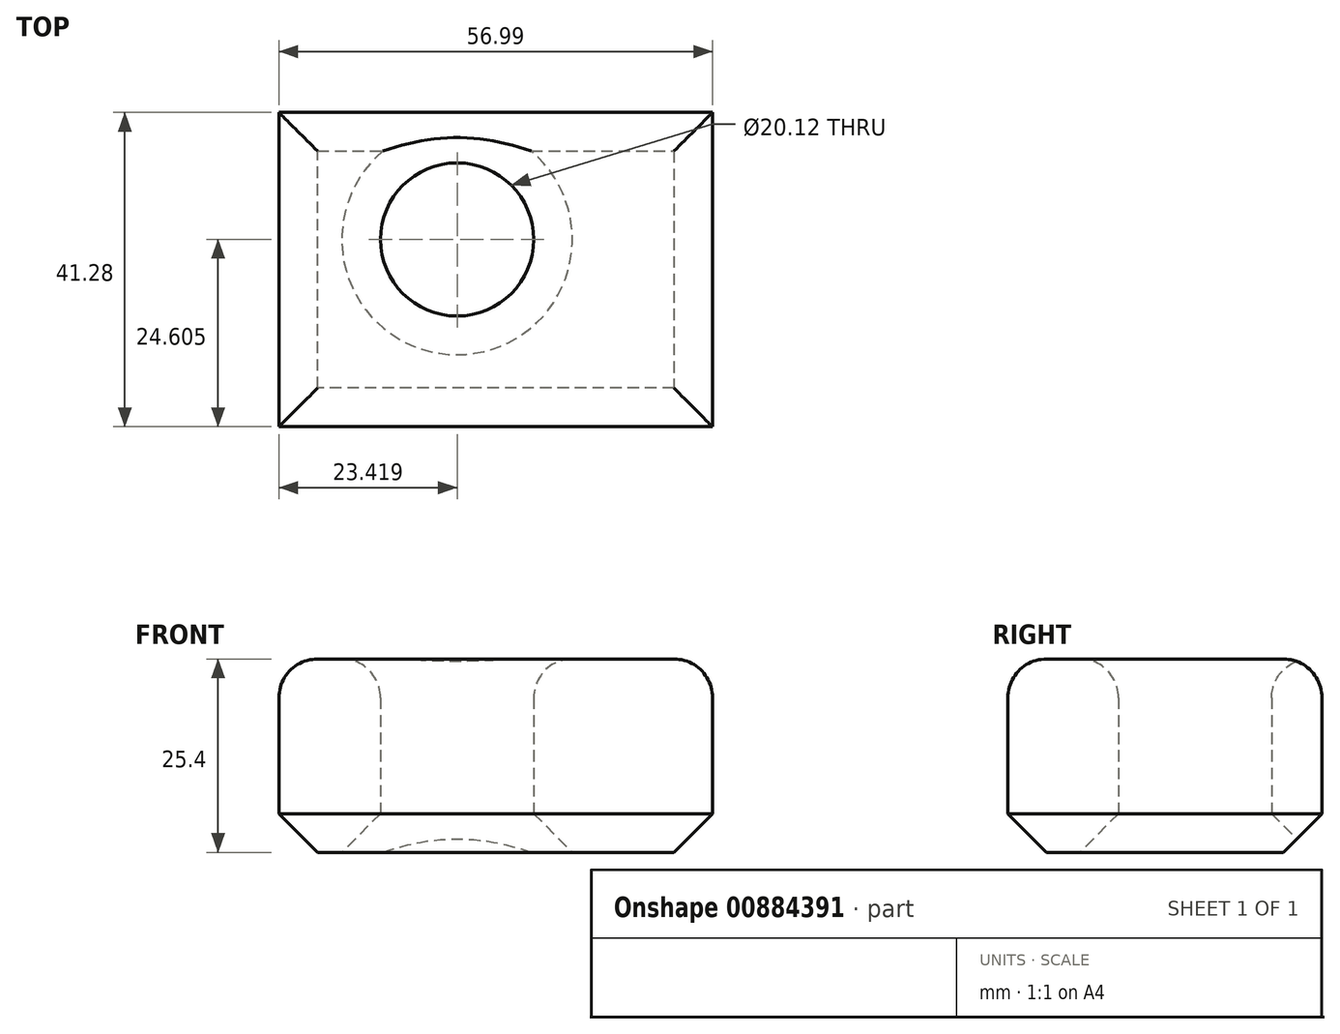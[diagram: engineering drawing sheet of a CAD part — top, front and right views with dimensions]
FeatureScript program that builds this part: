
annotation { "Feature Type Name" : "Feature", "Feature Type Description" : "" }
export const myFeature = defineFeature(function(context is Context, id is Id, definition is map)
    precondition{}
    {
        {
            var Q0;
            Q0=qCreatedBy(makeId("Top.planeOp"),FACE);
            var sketch = newSketch(context, id + "F0", { "sketchPlane" : qUnion([Q0])});
            skLineSegment(sketch, "E0.bottom", {"start": v(-66.58, 5.87) * mm, "end": v(-9.6, 5.87) * mm});
            skLineSegment(sketch, "E0.top", {"start": v(-66.58, -35.4) * mm, "end": v(-9.6, -35.4) * mm});
            skLineSegment(sketch, "E0.left", {"start": v(-66.58, 5.87) * mm, "end": v(-66.58, -35.4) * mm});
            skLineSegment(sketch, "E0.right", {"start": v(-9.6, 5.87) * mm, "end": v(-9.6, -35.4) * mm});
            skCircle(sketch, "E1", {"center": v(-43.16, -10.8) * mm, "radius": 10.06 * mm});
            skSolve(sketch);
        }
        {
            var Q0;
            Q0 = qSketchRegion(id + "F0", true);
            extrude(context, id + "F1", {"entities" : qUnion([Q0]), "depth" : 25.4 * mm, "offsetDistance" : 25.4 * mm});
        }
        {
            var Q0;
            Q0=makeQuery(id+"F1.opExtrude","CAP_FACE",FACE,{"disambiguationData":[OSD([sQuery(id+"F0.wireOp",EDGE,"E0.bottom"),sQuery(id+"F0.wireOp",EDGE,"E0.top"),sQuery(id+"F0.wireOp",EDGE,"E0.left"),sQuery(id+"F0.wireOp",EDGE,"E0.right"),sQuery(id+"F0.wireOp",EDGE,"E1")])],"isStart":false});
            fillet(context, id + "F2", {"entities" : qUnion([Q0]), "radius" : 5.08 * mm, "tangentPropagation" : true, "allowEdgeOverflow" : false});
        }
        {
            var Q0;
            Q0=makeQuery(id+"F1.opExtrude","CAP_FACE",FACE,{"disambiguationData":[OSD([sQuery(id+"F0.wireOp",EDGE,"E0.bottom"),sQuery(id+"F0.wireOp",EDGE,"E0.top"),sQuery(id+"F0.wireOp",EDGE,"E0.left"),sQuery(id+"F0.wireOp",EDGE,"E0.right"),sQuery(id+"F0.wireOp",EDGE,"E1")])],"isStart":true});
            chamfer(context, id + "F3", {"entities" : qUnion([Q0]), "width" : 5.08 * mm, "tangentPropagation" : true});
        }
    });
